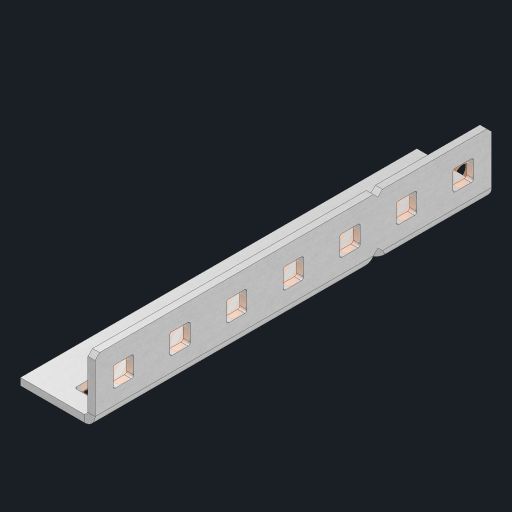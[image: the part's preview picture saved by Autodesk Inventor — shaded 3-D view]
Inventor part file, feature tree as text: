
AUTODESK INVENTOR PART (.ipt)
format: ipt  version: 2023 (Build 270158000, 158)  size: 531,968 bytes
history: native  units: in
note: dims shown in document units (in); Inventor stores cm internally (conversion verified against a paired STEP export)
features: other x19, extrude x13, sheet_metal_op x10, sketch x8, mirror x1, pattern_linear x1, chamfer x1
ambient origin geometry x8: Origin, YZ Plane, XZ Plane, XY Plane, X Axis, Y Axis, Z Axis, Center Point
bodies: Solid1 (feature_tree), Body (feature_tree)
feature tree (53):
  other  "Flange Pattern Plane"
  sheet_metal_op  "Flange Pattern"
  sheet_metal_op  "Body Pattern"
  other  "Arc Length"
  mirror  "Notch Mirror"
  pattern_linear  "Notch Pattern"  Spacing1=0.25in  [1 undecoded]
  chamfer  "End Chamfer"
  extrude  "Half Cut"  Depth=0.0625in
  sketch  "Sketch1"  dims[d0=1.5in]
  other  "Plate1"
  sketch  "Sketch2"  dims[d1=3.5in]
  other  "Plate2"
  sheet_metal_op  "Bend1"
  sheet_metal_op  "Corner1"
  sketch  "Sketch3"  dims[d2=0.0625in]
  other  "Flange Pattern Sketch"
  sketch  "Sketch7"  dims[d3=0.0625in]
  other  "Srf1"
  other  "Srf2"
  sketch  "Sketch8"  dims[d4=0.0312in]
  sketch  "Sketch9"  dims[d5=0.125in]
  other  "Srf91"
  sheet_metal_op  "Body Pattern Sketch"
  other  "Srf92"
  sketch  "Sketch13"  dims[d6=0.0625in]
  sketch  "Sketch14"  dims[d7=0.5in d8=90.0deg d9=0.0312in d10=0.25in d11=0.0625in d12=0.0625in d16=0.182in d17=0.02in d18=0.0625in d19=0.0in d20=0.25in d21=0.25in d46=0.172in d47=1.0in d48=0.0in d49=0.182in d50=0.02in d51=0.25in d52=0.25in d53=0.0625in d54=0.0in d55=0.172in d56=1.0in d57=0.0in d60=2.7559in d62=0.5in d63=0.3937in d65=0.5in d85=0.1473in d86=0.1782in d88=0.04in d89=0.0625in d90=0.0in d91=0.04in d92=0.0491in d95=2.5in d96=0.04in d97=0.25in d98=45.0deg d101=0.0in d102=2.497in d131=0.5in d132=2.7559in d134=0.5in d139=0.5in]
  other  "Srf856"
  other  "Srf1310"
  other  "Srf1311"
  other  "Srf1312"
  other  "Srf1376"
  other  "Srf1377"
  other  "Srf1728"
  other  "Srf1755"
  other  "Srf1878"
  other  "Srf1942"
  sheet_metal_op  "Flange Stamp"
  sheet_metal_op  "Flange Circle"
  sheet_metal_op  "Body Stamp"
  sheet_metal_op  "Body Circle"
  sheet_metal_op  "Notch"
  extrude  "ExtrusionSrf2"  Depth=0.0625in
  extrude  "ExtrusionSrf92"  Depth=0.5in
  extrude  "ExtrusionSrf856"  Depth=0.02in
  extrude  "ExtrusionSrf1310"  Depth=0.0625in
  extrude  "ExtrusionSrf1311"  TaperAngle=0.0deg  [1 undecoded]
  extrude  "ExtrusionSrf1312"  Depth=0.5in
  extrude  "ExtrusionSrf1376"  Depth=0.5in
  extrude  "ExtrusionSrf1377"  Depth=0.5in
  extrude  "ExtrusionSrf1728"  Depth=0.5in TaperAngle=0.0deg
  extrude  "ExtrusionSrf1755"  Depth=0.5in
  extrude  "ExtrusionSrf1878"  Depth=0.02in
  extrude  "ExtrusionSrf1942"  Depth=0.5in
note: 2 required parameter values undecoded (feature->parameter linkage not recoverable at this tier; creation-order binding heuristic only, values carry confidence <= 0.55)
